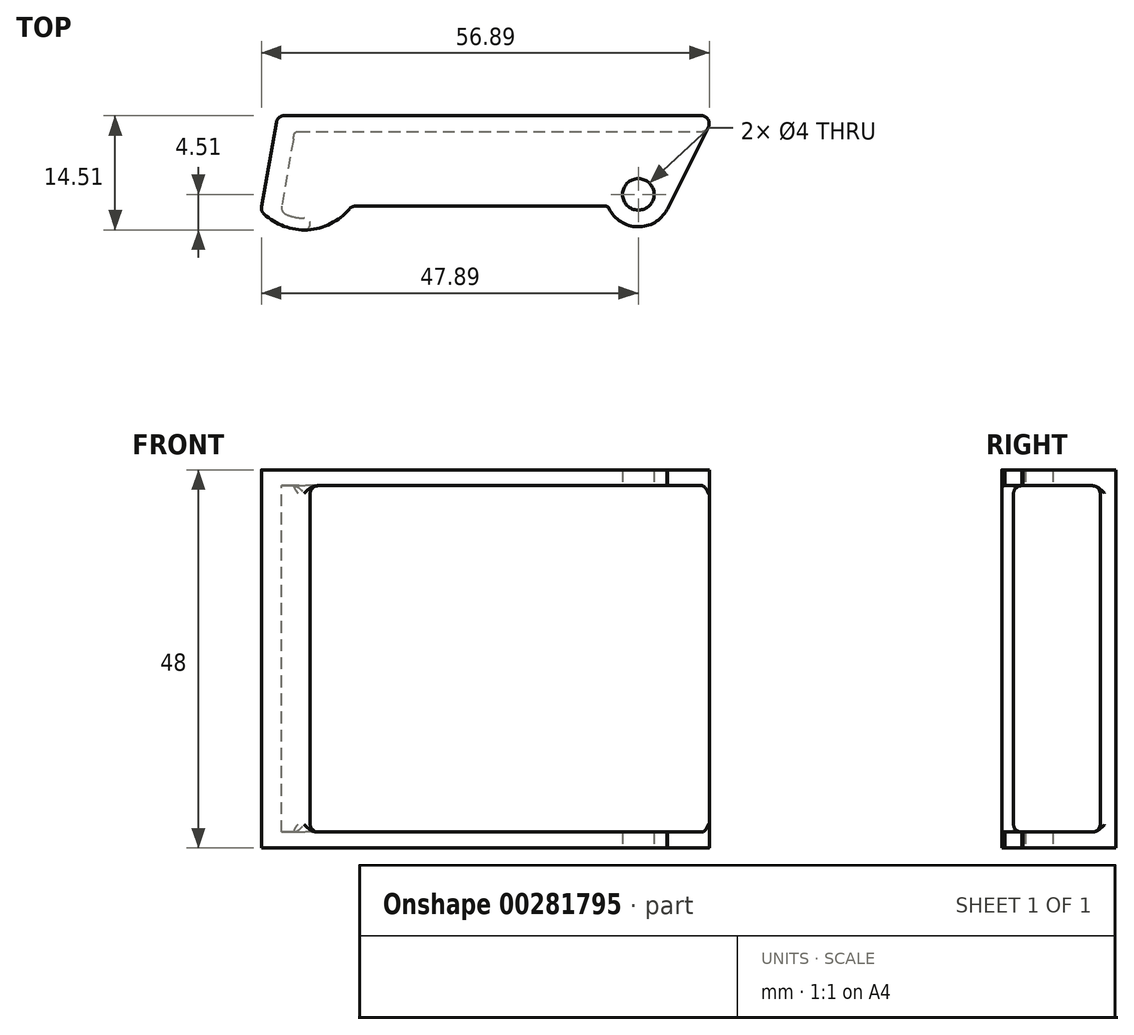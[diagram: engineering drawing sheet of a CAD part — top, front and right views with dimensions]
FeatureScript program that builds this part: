
annotation { "Feature Type Name" : "Feature", "Feature Type Description" : "" }
export const myFeature = defineFeature(function(context is Context, id is Id, definition is map)
    precondition{}
    {
        {
            var Q0;
            Q0=qCreatedBy(makeId("Top.planeOp"),FACE);
            var sketch = newSketch(context, id + "F0", { "sketchPlane" : qUnion([Q0])});
            skCircle(sketch, "E0", {"center": v(0, 0) * mm, "radius": 2 * mm});
            skLineSegment(sketch, "E1", {"start": v(0, 8) * mm, "end": v(-43.23, 8) * mm});
            skLineSegment(sketch, "E2", {"start": v(0, 10) * mm, "end": v(-42.5, 10) * mm});
            skArc(sketch, "E3", {"start": v(-42.44, -4.51) * mm, "mid": v(-41.69, -3.76) * mm, "end": v(-42.44, -3.01) * mm});
            skArc(sketch, "E4", {"start": v(8, 10) * mm, "mid": v(9, 9) * mm, "end": v(8, 8) * mm});
            skLineSegment(sketch, "E5", {"start": v(0, 8) * mm, "end": v(8, 8) * mm});
            skLineSegment(sketch, "E6", {"start": v(-35.95, -1.5) * mm, "end": v(-4.16, -1.5) * mm});
            skPoint(sketch, "E7.start.orphan", {"position": v(-42.44, -4.51) * mm});
            skLineSegment(sketch, "E8", {"start": v(-42.44, 2.99) * mm, "end": v(-42.44, -4.51) * mm, "construction": true});
            skArc(sketch, "E9", {"start": v(-3.71, -1.78) * mm, "mid": v(-0.09, -4.12) * mm, "end": v(3.63, -1.94) * mm});
            skArc(sketch, "E10", {"start": v(3.63, -1.94) * mm, "mid": v(0.24, 4.11) * mm, "end": v(-3.83, -1.5) * mm, "construction": true});
            skLineSegment(sketch, "E11", {"start": v(8, 10) * mm, "end": v(8, 8) * mm, "construction": true});
            skLineSegment(sketch, "E12", {"start": v(-43.72, 7.59) * mm, "end": v(-45.32, -1.47) * mm});
            skLineSegment(sketch, "E13", {"start": v(-45.98, 9.17) * mm, "end": v(-47.88, -1.57) * mm});
            skPoint(sketch, "E14.visualSharp", {"position": v(-43.65, 8) * mm});
            skArc(sketch, "E14.filletArc", {"start": v(-43.23, 8) * mm, "mid": v(-43.55, 7.88) * mm, "end": v(-43.72, 7.59) * mm});
            skPoint(sketch, "E15.visualSharp", {"position": v(-3.83, -1.5) * mm});
            skArc(sketch, "E15.filletArc", {"start": v(-3.71, -1.78) * mm, "mid": v(-3.9, -1.58) * mm, "end": v(-4.16, -1.5) * mm});
            skLineSegment(sketch, "E16", {"start": v(8, 10) * mm, "end": v(0, 10) * mm});
            skLineSegment(sketch, "E17", {"start": v(-42.5, 10) * mm, "end": v(-45, 10) * mm});
            skPoint(sketch, "E18.visualSharp", {"position": v(-45.84, 10) * mm});
            skArc(sketch, "E18.filletArc", {"start": v(-45, 10) * mm, "mid": v(-45.64, 9.77) * mm, "end": v(-45.98, 9.17) * mm});
            skArc(sketch, "E19", {"start": v(-42.44, -3.01) * mm, "mid": v(-43.6, -2.9) * mm, "end": v(-44.71, -2.56) * mm});
            skArc(sketch, "E20", {"start": v(-42.44, -4.51) * mm, "mid": v(-45.2, -3.98) * mm, "end": v(-47.58, -2.48) * mm});
            skArc(sketch, "E21", {"start": v(-42.44, -4.51) * mm, "mid": v(-39.28, -3.82) * mm, "end": v(-36.71, -1.85) * mm});
            skLineSegment(sketch, "E22", {"start": v(3.68, -1.85) * mm, "end": v(8.9, 8.55) * mm});
            skLineSegment(sketch, "E23", {"start": v(3.68, -1.85) * mm, "end": v(3.63, -1.94) * mm});
            skPoint(sketch, "E24.visualSharp", {"position": v(-45.45, -2.2) * mm});
            skArc(sketch, "E24.filletArc", {"start": v(-45.32, -1.47) * mm, "mid": v(-45.2, -2.12) * mm, "end": v(-44.71, -2.56) * mm});
            skPoint(sketch, "E25.visualSharp", {"position": v(-47.97, -2.08) * mm});
            skArc(sketch, "E25.filletArc", {"start": v(-47.88, -1.57) * mm, "mid": v(-47.84, -2.06) * mm, "end": v(-47.58, -2.48) * mm});
            skPoint(sketch, "E26.visualSharp", {"position": v(-36.43, -1.5) * mm});
            skArc(sketch, "E26.filletArc", {"start": v(-35.95, -1.5) * mm, "mid": v(-36.37, -1.6) * mm, "end": v(-36.71, -1.85) * mm});
            skSolve(sketch);
        }
        {
            var Q0;
            Q0 = qSketchRegion(id + "F0", true);
            extrude(context, id + "F1", {"entities" : qUnion([Q0]), "endBound" : BoundingType.SYMMETRIC, "depth" : 48 * mm});
        }
        {
            var Q0;
            Q0=makeQuery(id+"F0.imprint","IMPRINT",FACE,{"disambiguationData":[TD([[makeQuery(id+"F0.imprint","IMPRINT",EDGE,{"derivedFrom":sQuery(id+"F0.wireOp",EDGE,"E0")}),-1.0]])]});
            extrude(context, id + "F2", {"entities" : qUnion([Q0]), "operationType" : NewBodyOperationType.REMOVE, "endBound" : BoundingType.SYMMETRIC, "oppositeDirection" : true, "depth" : 44 * mm});
        }
        {
            var Q0;
            Q0=makeQuery(id+"F2.boolean.opBoolean","COPY",EDGE,{"derivedFrom":makeQuery(id+"F2.opExtrude","CAP_EDGE",EDGE,{"disambiguationData":[OSD([sQuery(id+"F0.wireOp",EDGE,"E1"),sQuery(id+"F0.wireOp",EDGE,"E5")])],"isStart":false})});
            var Q1;
            Q1=makeQuery(id+"F2.boolean.opBoolean","COPY",EDGE,{"derivedFrom":makeQuery(id+"F2.opExtrude","CAP_EDGE",EDGE,{"disambiguationData":[OSD([sQuery(id+"F0.wireOp",EDGE,"f4dc876b-5c7d-4906-accd-abf240a7ed24")])],"isStart":false})});
            var Q2;
            Q2=makeQuery(id+"F2.boolean.opBoolean","COPY",EDGE,{"derivedFrom":makeQuery(id+"F2.opExtrude","CAP_EDGE",EDGE,{"disambiguationData":[OSD([sQuery(id+"F0.wireOp",EDGE,"E3")])],"isStart":false})});
            var Q3;
            Q3=makeQuery(id+"F2.boolean.opBoolean","COPY",EDGE,{"derivedFrom":makeQuery(id+"F2.opExtrude","CAP_EDGE",EDGE,{"disambiguationData":[OSD([sQuery(id+"F0.wireOp",EDGE,"E4")])],"isStart":false})});
            var Q4;
            Q4=makeQuery(id+"F2.boolean.opBoolean","COPY",EDGE,{"derivedFrom":makeQuery(id+"F2.opExtrude","CAP_EDGE",EDGE,{"disambiguationData":[OSD([sQuery(id+"F0.wireOp",EDGE,"E4")])],"isStart":true})});
            var Q5;
            Q5=makeQuery(id+"F2.boolean.opBoolean","COPY",EDGE,{"derivedFrom":makeQuery(id+"F2.opExtrude","CAP_EDGE",EDGE,{"disambiguationData":[OSD([sQuery(id+"F0.wireOp",EDGE,"E1"),sQuery(id+"F0.wireOp",EDGE,"E5")])],"isStart":true})});
            var Q6;
            Q6=makeQuery(id+"F2.boolean.opBoolean","COPY",EDGE,{"derivedFrom":makeQuery(id+"F2.opExtrude","CAP_EDGE",EDGE,{"disambiguationData":[OSD([sQuery(id+"F0.wireOp",EDGE,"f4dc876b-5c7d-4906-accd-abf240a7ed24")])],"isStart":true})});
            var Q7;
            Q7=makeQuery(id+"F2.boolean.opBoolean","COPY",EDGE,{"derivedFrom":makeQuery(id+"F2.opExtrude","CAP_EDGE",EDGE,{"disambiguationData":[OSD([sQuery(id+"F0.wireOp",EDGE,"E3")])],"isStart":true})});
            fillet(context, id + "F3", {"entities" : qUnion([Q0, Q1, Q2, Q3, Q4, Q5, Q6, Q7]), "radius" : 1 * mm, "allowEdgeOverflow" : false});
        }
    });
